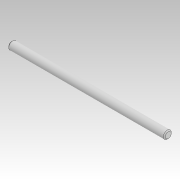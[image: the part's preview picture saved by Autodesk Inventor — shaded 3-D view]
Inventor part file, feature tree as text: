
AUTODESK INVENTOR PART (.ipt)
format: ipt  version: 2020 (Build 240168000, 168)  size: 83,968 bytes
history: native  units: mm
features: revolve x1, sketch x1
ambient origin geometry x8: Origin, YZ Plane, XZ Plane, XY Plane, X Axis, Y Axis, Z Axis, Center Point
bodies: Solid1 (feature_tree)
feature tree (2):
  revolve  "Revolution1"  Angle=135.0deg
  sketch  "Sketch1"  dims[d0=4.0mm d1=135.0deg d2=1.0mm d3=160.0mm d4=90.0deg]
